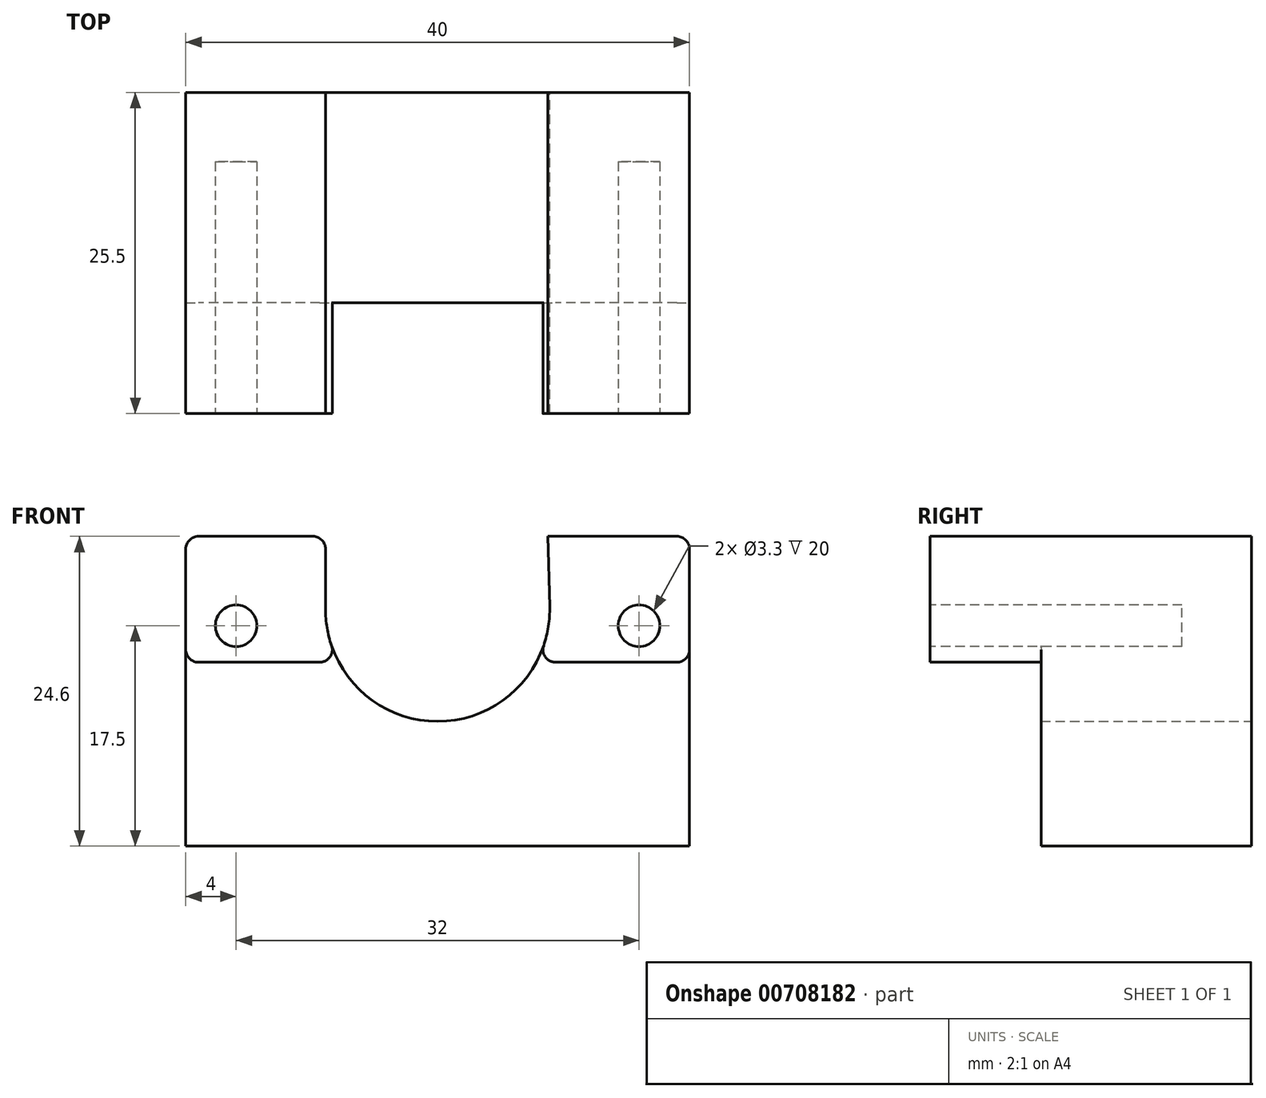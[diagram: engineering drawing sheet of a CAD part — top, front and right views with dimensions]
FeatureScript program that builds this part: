
annotation { "Feature Type Name" : "Feature", "Feature Type Description" : "" }
export const myFeature = defineFeature(function(context is Context, id is Id, definition is map)
    precondition{}
    {
        {
            var Q0;
            Q0=qCreatedBy(makeId("Right.planeOp"),FACE);
            var sketch = newSketch(context, id + "F0", { "sketchPlane" : qUnion([Q0])});
            skLineSegment(sketch, "E0", {"start": v(-8.8, 10) * mm, "end": v(16.7, 10) * mm});
            skLineSegment(sketch, "E1", {"start": v(16.7, 10) * mm, "end": v(16.7, -14.6) * mm});
            skLineSegment(sketch, "E2", {"start": v(16.7, -14.6) * mm, "end": v(0, -14.6) * mm});
            skLineSegment(sketch, "E3", {"start": v(0, -14.6) * mm, "end": v(0, 0) * mm});
            skLineSegment(sketch, "E4", {"start": v(0, 0) * mm, "end": v(-8.8, 0) * mm});
            skLineSegment(sketch, "E5", {"start": v(-8.8, 0) * mm, "end": v(-8.8, 10) * mm});
            skSolve(sketch);
        }
        {
            var Q0;
            Q0=qSketchRegion(id+"F0",true);
            extrude(context, id + "F1", {"entities" : qUnion([Q0]), "depth" : 40 * mm});
        }
        {
            var Q0;
            Q0=makeQuery(id+"F1.opExtrude","SWEPT_FACE",FACE,{"disambiguationData":[OSD([sQuery(id+"F0.wireOp",EDGE,"E5")])]});
            var sketch = newSketch(context, id + "F2", { "sketchPlane" : qUnion([Q0])});
            skLineSegment(sketch, "E6", {"start": v(20, 0) * mm, "end": v(20, 2.9) * mm, "construction": true});
            skLineSegment(sketch, "E7", {"start": v(4, 2.9) * mm, "end": v(36, 2.9) * mm, "construction": true});
            skCircle(sketch, "E8", {"center": v(4, 2.9) * mm, "radius": 1.65 * mm});
            skCircle(sketch, "E9.0.MirrorC", {"center": v(36, 2.9) * mm, "radius": 1.65 * mm});
            skSolve(sketch);
        }
        {
            var Q0;
            Q0=qSketchRegion(id+"F2",true);
            extrude(context, id + "F3", {"entities" : qUnion([Q0]), "operationType" : NewBodyOperationType.REMOVE, "oppositeDirection" : true, "depth" : 20 * mm});
        }
        {
            var Q0;
            Q0=makeQuery(id+"F1.opExtrude","SWEPT_FACE",FACE,{"disambiguationData":[OSD([sQuery(id+"F0.wireOp",EDGE,"E1")])]});
            var sketch = newSketch(context, id + "F4", { "sketchPlane" : qUnion([Q0])});
            skLineSegment(sketch, "E10", {"start": v(-20, 0) * mm, "end": v(-20, 4.2) * mm, "construction": true});
            skArc(sketch, "E11", {"start": v(-28.9, 4.41) * mm, "mid": v(-20.1, -4.7) * mm, "end": v(-11.1, 4.2) * mm});
            skLineSegment(sketch, "E12", {"start": v(-11.1, 4.2) * mm, "end": v(-11.1, 10) * mm});
            skLineSegment(sketch, "E13", {"start": v(-28.9, 4.41) * mm, "end": v(-28.76, 10) * mm});
            skLineSegment(sketch, "E14", {"start": v(-28.76, 10) * mm, "end": v(-11.1, 10) * mm});
            skSolve(sketch);
        }
        {
            var Q0;
            Q0=makeQuery(id+"F4.imprint","IMPRINT",FACE,{"disambiguationData":[TD([[makeQuery(id+"F4.imprint","IMPRINT",EDGE,{"derivedFrom":sQuery(id+"F4.wireOp",EDGE,"E11")}),1.0]])]});
            var Q1;
            Q1=makeQuery(id+"F1.opExtrude","SWEPT_FACE",FACE,{"disambiguationData":[OSD([sQuery(id+"F0.wireOp",EDGE,"E5")])]});
            extrude(context, id + "F5", {"entities" : qUnion([Q0]), "operationType" : NewBodyOperationType.REMOVE, "endBound" : BoundingType.UP_TO_SURFACE, "oppositeDirection" : true, "endBoundEntityFace" : qUnion([Q1]), "depth" : 25 * mm});
        }
        {
            var Q0;
            Q0=makeQuery(id+"F1.opExtrude","CAP_EDGE",EDGE,{"disambiguationData":[OSD([sQuery(id+"F0.wireOp",EDGE,"E0")])],"isStart":true});
            var Q1;
            Q1=makeQuery(id+"F1.opExtrude","CAP_EDGE",EDGE,{"disambiguationData":[OSD([sQuery(id+"F0.wireOp",EDGE,"E0")])],"isStart":false});
            var Q2;
            Q2=makeQuery(id+"F1.opExtrude","CAP_EDGE",EDGE,{"disambiguationData":[OSD([sQuery(id+"F0.wireOp",EDGE,"E4")])],"isStart":false});
            var Q3;
            Q3=makeQuery(id+"F1.opExtrude","CAP_EDGE",EDGE,{"disambiguationData":[OSD([sQuery(id+"F0.wireOp",EDGE,"E4")])],"isStart":true});
            var Q4;
            Q4=makeQuery(id+"F5.boolean.opBoolean","INTERSECT",EDGE,{"disambiguationData":[OD(0.0)],"derivedFrom":[makeQuery(id+"F1.opExtrude","SWEPT_FACE",FACE,{"disambiguationData":[OSD([sQuery(id+"F0.wireOp",EDGE,"E4")])]}),makeQuery(id+"F5.opExtrude","SWEPT_FACE",FACE,{"disambiguationData":[OSD([sQuery(id+"F4.wireOp",EDGE,"E11")])]})]});
            var Q5;
            Q5=makeQuery(id+"F5.boolean.opBoolean","INTERSECT",EDGE,{"disambiguationData":[OD(1.0)],"derivedFrom":[makeQuery(id+"F1.opExtrude","SWEPT_FACE",FACE,{"disambiguationData":[OSD([sQuery(id+"F0.wireOp",EDGE,"E4")])]}),makeQuery(id+"F5.opExtrude","SWEPT_FACE",FACE,{"disambiguationData":[OSD([sQuery(id+"F4.wireOp",EDGE,"E11")])]})]});
            var Q6;
            Q6=makeQuery(id+"F5.boolean.opBoolean","COPY",EDGE,{"derivedFrom":makeQuery(id+"F5.opExtrude","SWEPT_EDGE",EDGE,{"disambiguationData":[OSD([sQuery(id+"F0.wireOp",EDGE,"E0"),sQuery(id+"F0.wireOp",EDGE,"E1"),sQuery(id+"F4.wireOp",EDGE,"E12"),sQuery(id+"F4.wireOp",EDGE,"E14")])]})});
            var Q7;
            Q7=makeQuery(id+"F5.boolean.opBoolean","COPY",EDGE,{"derivedFrom":makeQuery(id+"F5.opExtrude","SWEPT_EDGE",EDGE,{"disambiguationData":[OSD([sQuery(id+"F0.wireOp",EDGE,"E0"),sQuery(id+"F0.wireOp",EDGE,"E1"),sQuery(id+"F4.wireOp",EDGE,"E13"),sQuery(id+"F4.wireOp",EDGE,"E14")])]})});
            fillet(context, id + "F6", {"entities" : qUnion([Q0, Q1, Q2, Q3, Q4, Q5, Q6, Q7]), "radius" : 1 * mm, "tangentPropagation" : true, "allowEdgeOverflow" : false});
        }
    });
